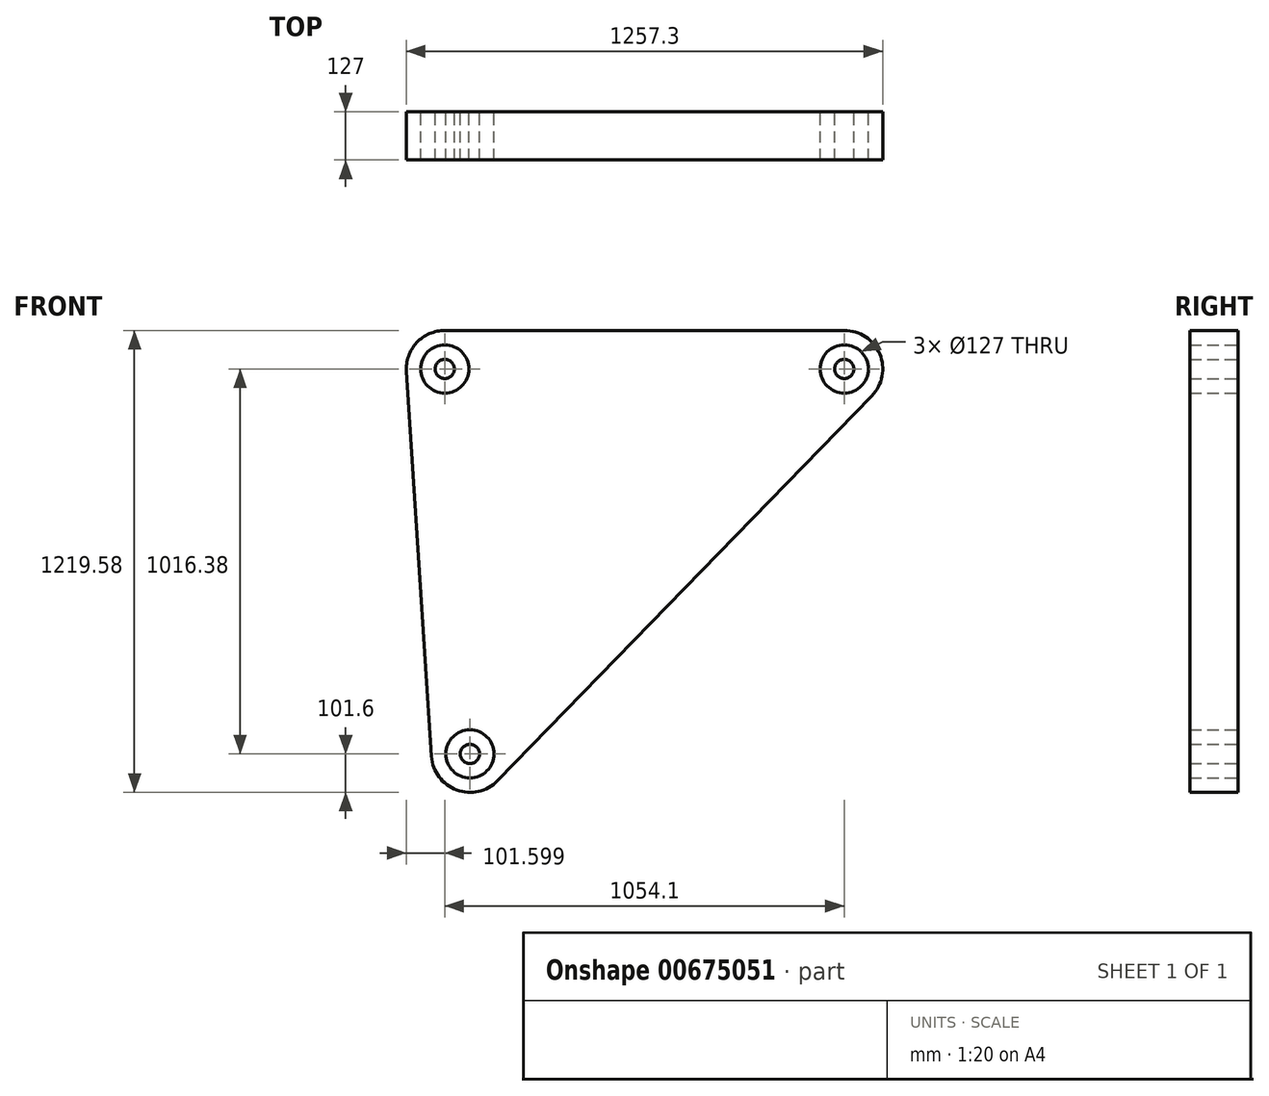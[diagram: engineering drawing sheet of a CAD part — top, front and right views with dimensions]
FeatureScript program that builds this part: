
annotation { "Feature Type Name" : "Feature", "Feature Type Description" : "" }
export const myFeature = defineFeature(function(context is Context, id is Id, definition is map)
    precondition{}
    {
        {
            var Q0;
            Q0=qCreatedBy(makeId("Front.planeOp"),FACE);
            var sketch = newSketch(context, id + "F0", { "sketchPlane" : qUnion([Q0])});
            skLineSegment(sketch, "E0", {"start": v(0, 0) * mm, "end": v(-66.3, 1016.38) * mm, "construction": true});
            skLineSegment(sketch, "E1", {"start": v(-66.3, 1016.38) * mm, "end": v(987.8, 1016.38) * mm, "construction": true});
            skLineSegment(sketch, "E2", {"start": v(987.8, 1016.38) * mm, "end": v(0, 0) * mm, "construction": true});
            skArc(sketch, "E3", {"start": v(-66.3, 1117.98) * mm, "mid": v(-140.43, 1085.85) * mm, "end": v(-167.68, 1009.77) * mm});
            skCircle(sketch, "E4", {"center": v(-66.3, 1016.38) * mm, "radius": 63.5 * mm});
            skCircle(sketch, "E5", {"center": v(-66.3, 1016.38) * mm, "radius": 25.4 * mm});
            skArc(sketch, "E6", {"start": v(1060.67, 945.57) * mm, "mid": v(1081.4, 1055.93) * mm, "end": v(987.8, 1117.98) * mm});
            skCircle(sketch, "E7", {"center": v(987.8, 1016.38) * mm, "radius": 63.5 * mm});
            skCircle(sketch, "E8", {"center": v(987.8, 1016.38) * mm, "radius": 25.4 * mm});
            skArc(sketch, "E9", {"start": v(-101.38, -6.61) * mm, "mid": v(-35.13, -95.34) * mm, "end": v(72.86, -70.81) * mm});
            skCircle(sketch, "E10", {"center": v(0, 0) * mm, "radius": 63.5 * mm});
            skCircle(sketch, "E11", {"center": v(0, 0) * mm, "radius": 25.4 * mm});
            skLineSegment(sketch, "E12", {"start": v(987.8, 1117.98) * mm, "end": v(-66.3, 1117.98) * mm});
            skLineSegment(sketch, "E13", {"start": v(-167.68, 1009.77) * mm, "end": v(-101.38, -6.61) * mm});
            skLineSegment(sketch, "E14", {"start": v(1060.67, 945.57) * mm, "end": v(72.86, -70.81) * mm});
            skSolve(sketch);
        }
        {
            var Q0;
            Q0=makeQuery(id+"F0.imprint","IMPRINT",FACE,{"disambiguationData":[TD([[makeQuery(id+"F0.imprint","IMPRINT",EDGE,{"derivedFrom":sQuery(id+"F0.wireOp",EDGE,"E3")}),1.0]])]});
            var Q1;
            Q1=makeQuery(id+"F0.imprint","IMPRINT",FACE,{"disambiguationData":[TD([[makeQuery(id+"F0.imprint","IMPRINT",EDGE,{"derivedFrom":sQuery(id+"F0.wireOp",EDGE,"E5")}),1.0]])]});
            var Q2;
            Q2=makeQuery(id+"F0.imprint","IMPRINT",FACE,{"disambiguationData":[TD([[makeQuery(id+"F0.imprint","IMPRINT",EDGE,{"derivedFrom":sQuery(id+"F0.wireOp",EDGE,"E11")}),1.0]])]});
            var Q3;
            Q3=makeQuery(id+"F0.imprint","IMPRINT",FACE,{"disambiguationData":[TD([[makeQuery(id+"F0.imprint","IMPRINT",EDGE,{"derivedFrom":sQuery(id+"F0.wireOp",EDGE,"E8")}),1.0]])]});
            extrude(context, id + "F1", {"entities" : qUnion([Q0, Q1, Q2, Q3]), "depth" : 127 * mm, "offsetDistance" : 25.4 * mm});
        }
    });
